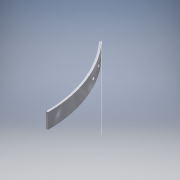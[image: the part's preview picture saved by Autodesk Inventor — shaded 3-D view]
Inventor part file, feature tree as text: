
AUTODESK INVENTOR PART (.ipt)
format: ipt  version: 2016 (Build 200138000, 138)  size: 119,296 bytes
history: native  units: in
note: dims shown in document units (in); Inventor stores cm internally (conversion verified against a paired STEP export)
features: extrude x2, sketch x2, plane x1
ambient origin geometry x8: Origin, YZ Plane, XZ Plane, XY Plane, X Axis, Y Axis, Z Axis, Center Point
bodies: Solid1 (feature_tree)
feature tree (5):
  extrude  "Extrusion1"  Depth=0.125in
  plane  "Work Plane1"
  extrude  "Extrusion2"  Depth=1.0in TaperAngle=0.0deg
  sketch  "Sketch1"  dims[d0=17.0in d1=0.125in]
  sketch  "Sketch2"  dims[d2=45.0deg d3=1.0in d4=0.0in d5=0.2656in d6=1.5in d7=0.2656in d8=0.75in d9=0.5in d10=0.5in d11=0.7in d12=0.0in]
